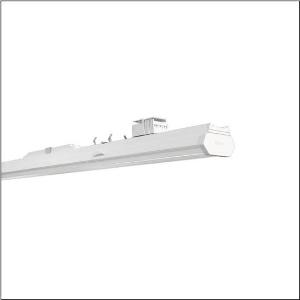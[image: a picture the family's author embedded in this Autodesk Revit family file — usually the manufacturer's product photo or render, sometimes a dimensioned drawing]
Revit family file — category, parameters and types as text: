
# Revit family: licross_r__21_protected_ho_52tp11cn4c5s_d46e
name_source: partatom
category: Lighting Fixtures
units: mm (PartAtom-declared; Revit-internal decimal feet)

## family parameters
Cut with Voids When Loaded = No
Host = Face
Light Source = No
Part Type = Normal
Room Calculation Point = No
Round Connector Dimension = Use Diameter
Shared = No

## types (1)
- --- (1 x LED, 12650 lm, 68.9 W, 4000K)
    Apparent Load = 69 VA
    CIE Flux Codes = 84 94 98 99 100
    Color Rendering = 80
    Color Temperature = 4000K
    Default Elevation = 1800 mm
    Description = Licross® 21 Protected HO, luminaire insert, of sheet steel, galvanised, coil coated, white, length: 1.500mm, width: 66mm, height: 67mm, LED rated luminous flux: 12.650lm, light colour: 840, SDCM (Standard Deviation of Colour Matching)MacAdam ≤ 3 SDCM (initial), control gear: ON/OFF Multilumen, CLOi, with plug, 3-pole, with phase selection, mains connection: 220..240V, AC, 50/60Hz, start of lifetime: 69W, end of service life: 83W, internal wiring halogen-free, primary light control with lens, of plastic, primary optical cover: cover, of PMMA, light emission: direct distribution, primary light characteristic: symmetric, protection rating (complete): IP64, insulation class (complete): insulation class I (protective earthing), certification: CE, ENEC, VDE, UKCA, protection symbol: D if used in an environment with conductive dust loads with corresponding accessories, impact resistance: IK06, permissible ambient temperature for indoor applications: -35..+35°C, corresponds to IFS (International Featured Standards) requirements for safety and quality in the food industry, reducing of maximum allowable ambient temperature of 5°C with ceiling mounting, LABS conformity tested according to VDMA 24364:2018-05, packaging unit: 1 piece
    Height = 92 mm
    Lamp = 1 x LED
    Lamp Light Flux = 12650 lm
    Lamp Power = 68.9 W
    Lamp count = 1
    Length = 1500 mm
    Luminous efficacy = 184 lm/W
    Manufacturer = Siteco
    ModVariant = No
    Model = 52TP11CN4C5S
    Mounting Place = Ceiling
    Mounting Type = Pendant
    Number of Poles = 1
    OnlyDefault = Yes
    Power Factor = 1
    Product Name = Licross® 21 Protected HO
    Product group = luminaire insert | ceiling pendant
    ProductGroupID = 901
    Protection Class = Protection class I
    Protection Degree = IP 64
    RLX_Detail_Level = 1
    RLX_Emergency_Light_Flux = 0 lm
    RLX_Emergency_Type = 0
    RLX_Emergency_Type_DB = No
    RlxData = <blob elided: 22153 chars, md5=21df5dca>
    Socket = socket
    Standby Power = 0 W
    System Light Flux = 12650 lm
    System Power = 69 W
    Type Comments = factory setting: luminous flux: 100 % | (A | C | E) | 162 mA
    Type Image = l_1256148.jpg
    URL = http://relux.com
    VarID = @adj_114799
    Voltage = 0 V
    Weight = 0.00 kg
    Width = 88 mm

## geometry (parser evidence)
native form markers: Blend x4, Sweep x13
no freeform markers — native parametric forms only
